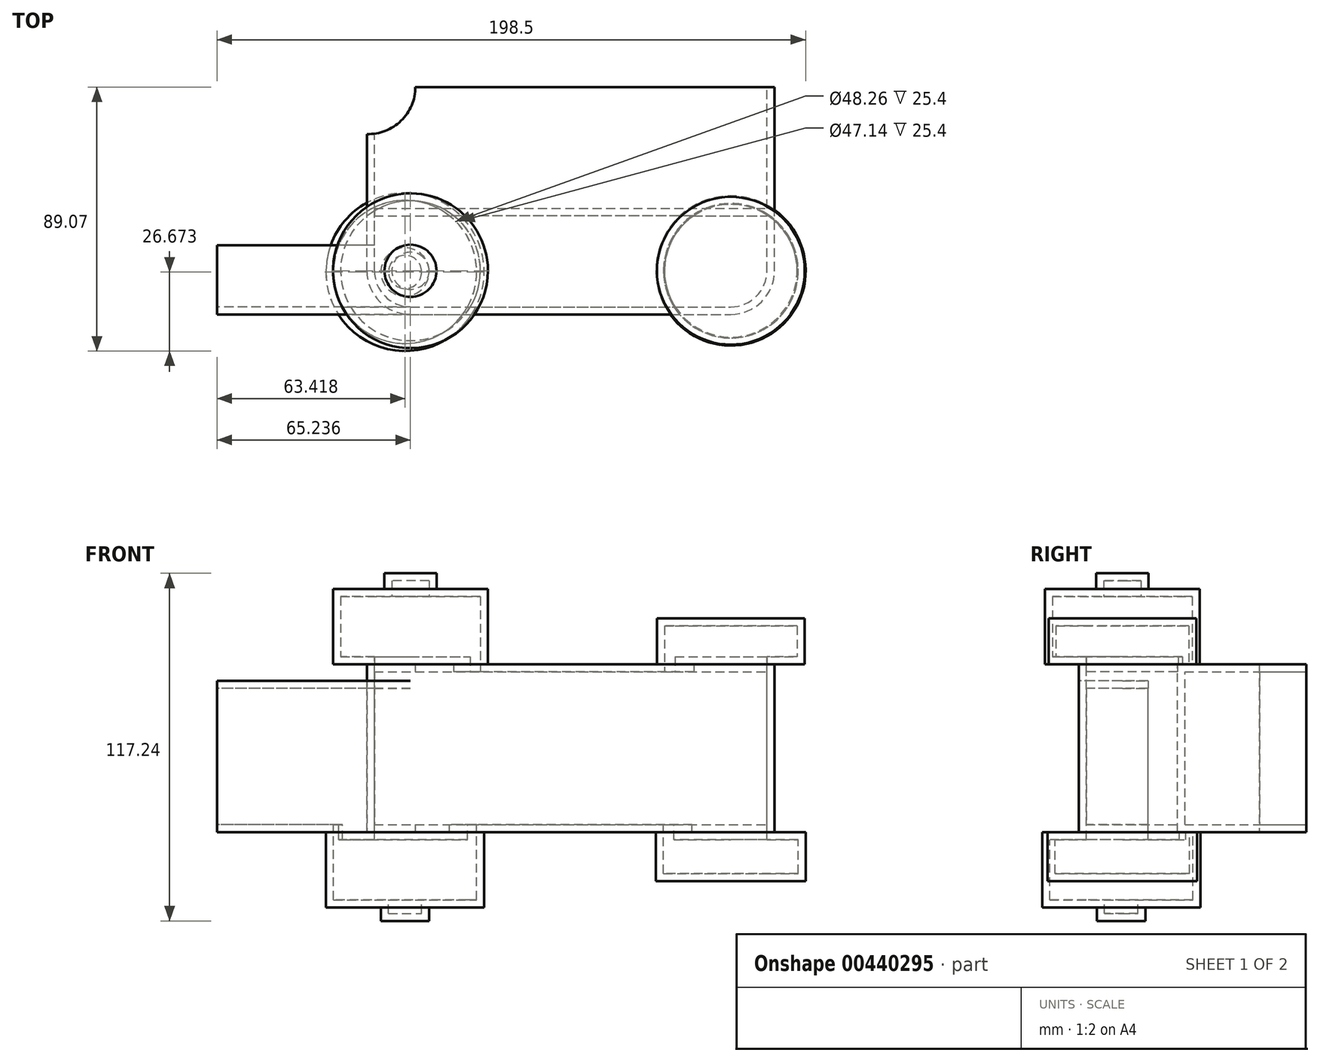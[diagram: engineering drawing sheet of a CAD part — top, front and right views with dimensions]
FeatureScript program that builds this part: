
annotation { "Feature Type Name" : "Feature", "Feature Type Description" : "" }
export const myFeature = defineFeature(function(context is Context, id is Id, definition is map)
    precondition{}
    {
        {
            var Q0;
            Q0=qCreatedBy(makeId("Front.planeOp"),FACE);
            var sketch = newSketch(context, id + "F0", { "sketchPlane" : qUnion([Q0])});
            skLineSegment(sketch, "E0.bottom", {"start": v(-66.75, 0) * mm, "end": v(70.71, 0) * mm});
            skLineSegment(sketch, "E0.top", {"start": v(-66.75, 56.54) * mm, "end": v(70.71, 56.54) * mm});
            skLineSegment(sketch, "E0.left", {"start": v(-66.75, 0) * mm, "end": v(-66.75, 56.54) * mm});
            skLineSegment(sketch, "E0.right", {"start": v(70.71, 0) * mm, "end": v(70.71, 56.54) * mm});
            skSolve(sketch);
        }
        {
            var Q0;
            Q0 = qSketchRegion(id + "F0", true);
            extrude(context, id + "F1", {"entities" : qUnion([Q0]), "depth" : 43.43 * mm});
        }
        {
            var Q0;
            Q0=qCreatedBy(makeId("Top.planeOp"),FACE);
            var sketch = newSketch(context, id + "F2", { "sketchPlane" : qUnion([Q0])});
            skLineSegment(sketch, "E1.bottom", {"start": v(70.33, 0) * mm, "end": v(-66.26, 0) * mm});
            skLineSegment(sketch, "E1.top", {"start": v(70.33, 29.74) * mm, "end": v(-66.26, 29.74) * mm});
            skLineSegment(sketch, "E1.left", {"start": v(70.33, 0) * mm, "end": v(70.33, 29.74) * mm});
            skLineSegment(sketch, "E1.right", {"start": v(-66.26, 0) * mm, "end": v(-66.26, 29.74) * mm});
            skSolve(sketch);
        }
        {
            var Q0;
            Q0=makeQuery(id+"F1.opExtrude","CAP_FACE",FACE,{"disambiguationData":[OSD([sQuery(id+"F0.wireOp",EDGE,"E0.bottom"),sQuery(id+"F0.wireOp",EDGE,"E0.top"),sQuery(id+"F0.wireOp",EDGE,"E0.left"),sQuery(id+"F0.wireOp",EDGE,"E0.right")])],"isStart":true});
            shell(context, id + "F3", {"entities" : qUnion([Q0]), "thickness" : 2.54 * mm});
        }
        {
            var Q0;
            Q0=makeQuery(id+"F1.opExtrude","CAP_FACE",FACE,{"disambiguationData":[OSD([sQuery(id+"F0.wireOp",EDGE,"E0.bottom"),sQuery(id+"F0.wireOp",EDGE,"E0.top"),sQuery(id+"F0.wireOp",EDGE,"E0.left"),sQuery(id+"F0.wireOp",EDGE,"E0.right")])],"isStart":false});
            var sketch = newSketch(context, id + "F4", { "sketchPlane" : qUnion([Q0])});
            skLineSegment(sketch, "E2.bottom", {"start": v(70.71, 0) * mm, "end": v(-66.75, 0) * mm});
            skLineSegment(sketch, "E2.top", {"start": v(70.71, 56.54) * mm, "end": v(-66.75, 56.54) * mm});
            skLineSegment(sketch, "E2.left", {"start": v(70.71, 0) * mm, "end": v(70.71, 56.54) * mm});
            skLineSegment(sketch, "E2.right", {"start": v(-66.75, 0) * mm, "end": v(-66.75, 56.54) * mm});
            skSolve(sketch);
        }
        {
            var Q0;
            Q0 = qSketchRegion(id + "F4", true);
            extrude(context, id + "F5", {"entities" : qUnion([Q0]), "operationType" : NewBodyOperationType.ADD, "depth" : 33.27 * mm});
        }
        {
            var Q0;
            Q0=makeQuery(id+"F5.opExtrude","CAP_EDGE",EDGE,{"disambiguationData":[OSD([sQuery(id+"F4.wireOp",EDGE,"E2.left")])],"isStart":false});
            var Q1;
            Q1=makeQuery(id+"F5.opExtrude","CAP_EDGE",EDGE,{"disambiguationData":[OSD([sQuery(id+"F4.wireOp",EDGE,"E2.right")])],"isStart":false});
            fillet(context, id + "F6", {"entities" : qUnion([Q0, Q1]), "radius" : 14.72 * mm, "tangentPropagation" : true, "allowEdgeOverflow" : false});
        }
        {
            var Q0;
            Q0=sQuery(id+"F2.wireOp",VERTEX,"E1.right.start");
            var Q1;
            Q1=makeQuery(id+"F1.opExtrude","SWEPT_BODY",BODY,{"disambiguationData":[OSD([sQuery(id+"F0.wireOp",EDGE,"E0.bottom"),sQuery(id+"F0.wireOp",EDGE,"E0.top"),sQuery(id+"F0.wireOp",EDGE,"E0.left"),sQuery(id+"F0.wireOp",EDGE,"E0.right")])]});
            hole(context, id + "F7", {"style" : HoleStyle.SIMPLE, "endStyle" : HoleEndStyle.BLIND, "oppositeDirection" : true, "holeDiameter" : 31.75 * mm, "holeDepth" : 139.7 * mm, "isTappedThrough" : true, "tappedDepth" : 12.7 * mm, "tapClearance" : 3, "locations" : qUnion([Q0]), "scope" : qUnion([Q1])});
        }
        {
            var Q0;
            Q0=makeQuery(id+"F5.boolean.opBoolean","MERGE",FACE,{"derivedFrom":[makeQuery(id+"F1.opExtrude","SWEPT_FACE",FACE,{"disambiguationData":[OSD([sQuery(id+"F0.wireOp",EDGE,"E0.bottom")])]}),makeQuery(id+"F5.opExtrude","SWEPT_FACE",FACE,{"disambiguationData":[OSD([sQuery(id+"F4.wireOp",EDGE,"E2.bottom")])]})]});
            var sketch = newSketch(context, id + "F8", { "sketchPlane" : qUnion([Q0])});
            skCircle(sketch, "E3", {"center": v(56, 62) * mm, "radius": 25.24 * mm});
            skSolve(sketch);
        }
        {
            var Q0;
            Q0 = qSketchRegion(id + "F8", true);
            extrude(context, id + "F9", {"entities" : qUnion([Q0]), "operationType" : NewBodyOperationType.ADD, "depth" : 16.5 * mm});
        }
        {
            var Q0;
            Q0=makeQuery(id+"F5.boolean.opBoolean","MERGE",FACE,{"derivedFrom":[makeQuery(id+"F1.opExtrude","SWEPT_FACE",FACE,{"disambiguationData":[OSD([sQuery(id+"F0.wireOp",EDGE,"E0.bottom")])]}),makeQuery(id+"F5.opExtrude","SWEPT_FACE",FACE,{"disambiguationData":[OSD([sQuery(id+"F4.wireOp",EDGE,"E2.bottom")])]})]});
            var sketch = newSketch(context, id + "F10", { "sketchPlane" : qUnion([Q0])});
            skSolve(sketch);
        }
        {
            var Q0;
            {var subQ2=sQuery(id+"F0.wireOp",EDGE,"E0.bottom");Q0=makeQuery(id+"F10.imprint","IMPRINT",FACE,{"disambiguationData":[TD([[makeQuery(id+"F10.imprint","IMPRINT",EDGE,{"derivedFrom":makeQuery(id+"F1.opExtrude","CAP_EDGE",EDGE,{"disambiguationData":[OSD([subQ2])],"isStart":true})}),1.0]])]});}
            var sketch = newSketch(context, id + "F11", { "sketchPlane" : qUnion([Q0])});
            skCircle(sketch, "E4", {"center": v(-53.85, 62.4) * mm, "radius": 26.67 * mm});
            skSolve(sketch);
        }
        {
            var Q0;
            Q0 = qSketchRegion(id + "F11", true);
            extrude(context, id + "F12", {"entities" : qUnion([Q0]), "operationType" : NewBodyOperationType.ADD, "depth" : 25.4 * mm});
        }
        {
            var Q0;
            Q0=makeQuery(id+"F5.boolean.opBoolean","MERGE",FACE,{"derivedFrom":[makeQuery(id+"F1.opExtrude","SWEPT_FACE",FACE,{"disambiguationData":[OSD([sQuery(id+"F0.wireOp",EDGE,"E0.top")])]}),makeQuery(id+"F5.opExtrude","SWEPT_FACE",FACE,{"disambiguationData":[OSD([sQuery(id+"F4.wireOp",EDGE,"E2.top")])]})]});
            var sketch = newSketch(context, id + "F13", { "sketchPlane" : qUnion([Q0])});
            skCircle(sketch, "E5", {"center": v(-52.03, -62) * mm, "radius": 26.1 * mm});
            skSolve(sketch);
        }
        {
            var Q0;
            Q0 = qSketchRegion(id + "F13", true);
            extrude(context, id + "F14", {"entities" : qUnion([Q0]), "operationType" : NewBodyOperationType.ADD, "depth" : 25.4 * mm});
        }
        {
            var Q0;
            Q0=makeQuery(id+"F5.boolean.opBoolean","MERGE",FACE,{"derivedFrom":[makeQuery(id+"F1.opExtrude","SWEPT_FACE",FACE,{"disambiguationData":[OSD([sQuery(id+"F0.wireOp",EDGE,"E0.top")])]}),makeQuery(id+"F5.opExtrude","SWEPT_FACE",FACE,{"disambiguationData":[OSD([sQuery(id+"F4.wireOp",EDGE,"E2.top")])]})]});
            var sketch = newSketch(context, id + "F15", { "sketchPlane" : qUnion([Q0])});
            skCircle(sketch, "E6", {"center": v(56, -62) * mm, "radius": 24.92 * mm});
            skSolve(sketch);
        }
        {
            var Q0;
            Q0 = qSketchRegion(id + "F15", true);
            extrude(context, id + "F16", {"entities" : qUnion([Q0]), "operationType" : NewBodyOperationType.ADD, "depth" : 15.5 * mm});
        }
        {
            var Q0;
            Q0=makeQuery(id+"F14.opExtrude","CAP_FACE",FACE,{"disambiguationData":[OSD([sQuery(id+"F13.wireOp",EDGE,"E5")])],"isStart":false});
            var sketch = newSketch(context, id + "F17", { "sketchPlane" : qUnion([Q0])});
            skCircle(sketch, "E7", {"center": v(-52.03, -62) * mm, "radius": 8.8 * mm});
            skSolve(sketch);
        }
        {
            var Q0;
            Q0 = qSketchRegion(id + "F17", true);
            extrude(context, id + "F18", {"entities" : qUnion([Q0]), "operationType" : NewBodyOperationType.ADD, "depth" : 5.33 * mm});
        }
        {
            var Q0;
            Q0=makeQuery(id+"F12.opExtrude","CAP_FACE",FACE,{"disambiguationData":[OSD([sQuery(id+"F11.wireOp",EDGE,"E4")])],"isStart":false});
            var sketch = newSketch(context, id + "F19", { "sketchPlane" : qUnion([Q0])});
            skCircle(sketch, "E8", {"center": v(-53.85, 62.4) * mm, "radius": 8.14 * mm});
            skSolve(sketch);
        }
        {
            var Q0;
            Q0 = qSketchRegion(id + "F19", true);
            extrude(context, id + "F20", {"entities" : qUnion([Q0]), "operationType" : NewBodyOperationType.ADD, "depth" : 4.57 * mm});
        }
        {
            var Q0;
            Q0=makeQuery(id+"F5.opExtrude","CAP_FACE",FACE,{"disambiguationData":[OSD([sQuery(id+"F4.wireOp",EDGE,"E2.bottom"),sQuery(id+"F4.wireOp",EDGE,"E2.top"),sQuery(id+"F4.wireOp",EDGE,"E2.left"),sQuery(id+"F4.wireOp",EDGE,"E2.right")])],"isStart":false});
            var sketch = newSketch(context, id + "F21", { "sketchPlane" : qUnion([Q0])});
            skLineSegment(sketch, "E9.bottom", {"start": v(-52.03, 50.97) * mm, "end": v(-117.27, 50.97) * mm});
            skLineSegment(sketch, "E9.top", {"start": v(-52.03, 0) * mm, "end": v(-117.27, 0) * mm});
            skLineSegment(sketch, "E9.left", {"start": v(-52.03, 50.97) * mm, "end": v(-52.03, 0) * mm});
            skLineSegment(sketch, "E9.right", {"start": v(-117.27, 50.97) * mm, "end": v(-117.27, 0) * mm});
            skSolve(sketch);
        }
        {
            var Q0;
            Q0 = qSketchRegion(id + "F21", true);
            extrude(context, id + "F22", {"entities" : qUnion([Q0]), "operationType" : NewBodyOperationType.ADD, "oppositeDirection" : true, "depth" : 23.37 * mm});
        }
        {
            var Q0;
            Q0=makeQuery(id+"F22.opExtrude","CAP_FACE",FACE,{"disambiguationData":[OSD([sQuery(id+"F21.wireOp",EDGE,"E9.bottom"),sQuery(id+"F21.wireOp",EDGE,"E9.top"),sQuery(id+"F21.wireOp",EDGE,"E9.left"),sQuery(id+"F21.wireOp",EDGE,"E9.right")])],"isStart":false});
            var Q1;
            Q1=makeQuery(id+"F22.opExtrude","SWEPT_FACE",FACE,{"disambiguationData":[OSD([sQuery(id+"F21.wireOp",EDGE,"E9.right")])]});
            shell(context, id + "F23", {"entities" : qUnion([Q0, Q1]), "thickness" : 2.54 * mm});
        }
    });
